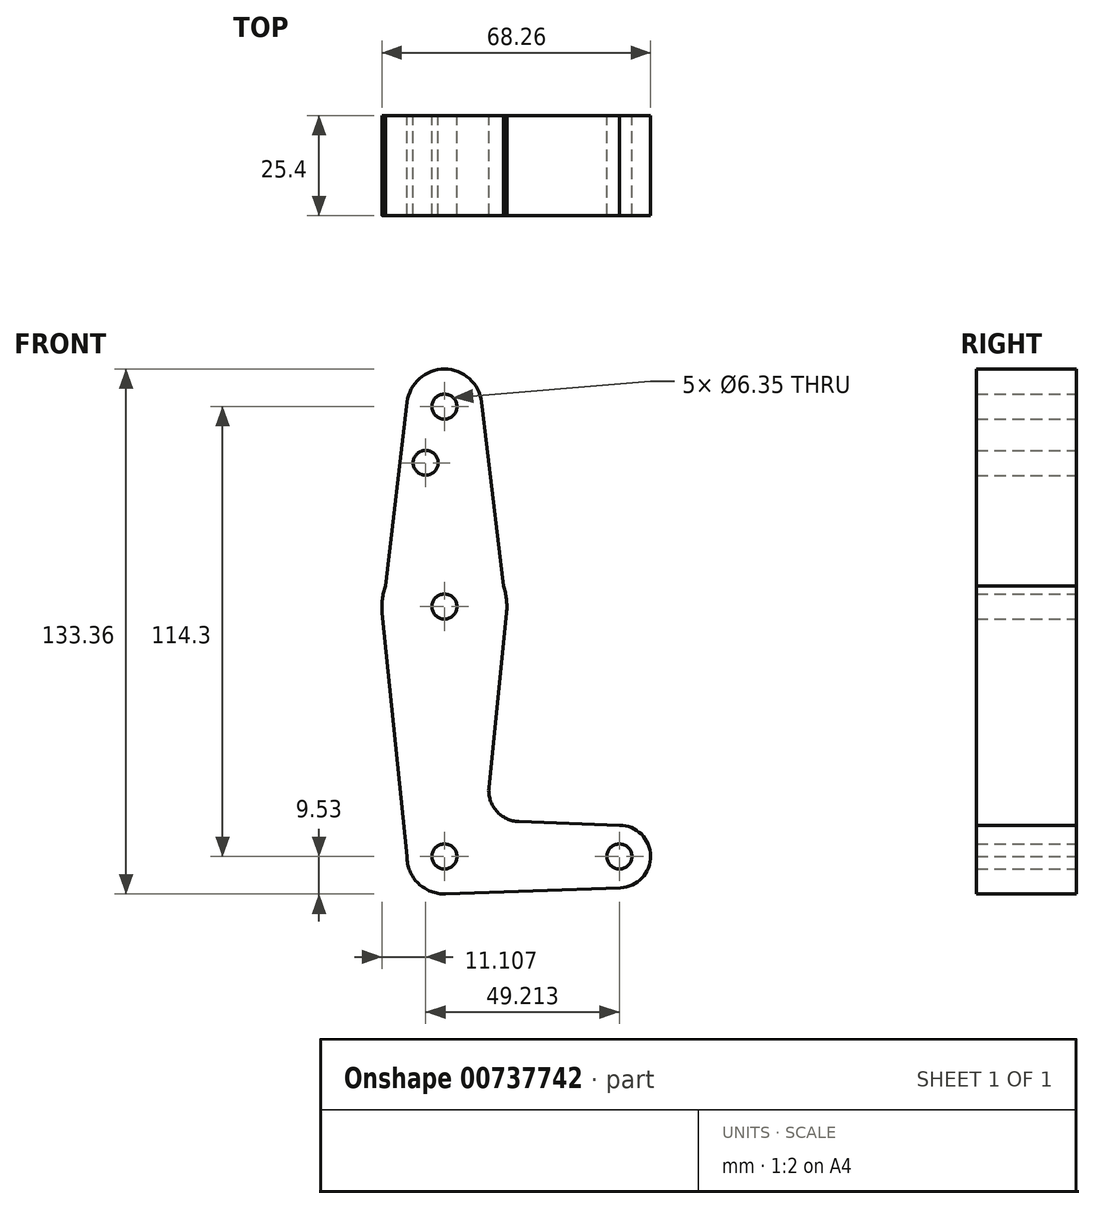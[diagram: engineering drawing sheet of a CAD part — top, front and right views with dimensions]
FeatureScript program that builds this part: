
annotation { "Feature Type Name" : "Feature", "Feature Type Description" : "" }
export const myFeature = defineFeature(function(context is Context, id is Id, definition is map)
    precondition{}
    {
        {
            var Q0;
            Q0=qCreatedBy(makeId("Front.planeOp"),FACE);
            var sketch = newSketch(context, id + "F0", { "sketchPlane" : qUnion([Q0])});
            skLineSegment(sketch, "E0", {"start": v(0, 0) * mm, "end": v(44.45, 0) * mm, "construction": true});
            skCircle(sketch, "E1", {"center": v(44.45, 0) * mm, "radius": 7.94 * mm});
            skPoint(sketch, "E2.orphan", {"position": v(0, 57.15) * mm});
            skPoint(sketch, "E3.center.orphan", {"position": v(0, 114.3) * mm});
            skLineSegment(sketch, "E4", {"start": v(0, 114.3) * mm, "end": v(0, 0) * mm, "construction": true});
            skCircle(sketch, "E5", {"center": v(0, 0) * mm, "radius": 9.53 * mm});
            skCircle(sketch, "E6", {"center": v(0, 114.3) * mm, "radius": 9.53 * mm});
            skPoint(sketch, "E7.orphan", {"position": v(0, -6.35) * mm});
            skCircle(sketch, "E8", {"center": v(0, 63.5) * mm, "radius": 15.88 * mm});
            skLineSegment(sketch, "E9", {"start": v(44.45, 7.94) * mm, "end": v(18.93, 8.85) * mm});
            skLineSegment(sketch, "E10", {"start": v(44.73, -7.93) * mm, "end": v(0, -9.53) * mm});
            skLineSegment(sketch, "E11", {"start": v(11.3, 17.6) * mm, "end": v(15.8, 61.9) * mm});
            skLineSegment(sketch, "E12", {"start": v(-9.52, 0) * mm, "end": v(-15.8, 61.9) * mm});
            skLineSegment(sketch, "E13", {"start": v(-15.8, 61.9) * mm, "end": v(-9.46, 115.42) * mm});
            skLineSegment(sketch, "E14", {"start": v(9.46, 115.42) * mm, "end": v(15.8, 61.9) * mm});
            skCircle(sketch, "E15", {"center": v(0, 114.3) * mm, "radius": 3.18 * mm});
            skCircle(sketch, "E16", {"center": v(-4.76, 100.03) * mm, "radius": 3.18 * mm});
            skCircle(sketch, "E17", {"center": v(0, 63.5) * mm, "radius": 3.18 * mm});
            skCircle(sketch, "E18", {"center": v(0, 0) * mm, "radius": 3.18 * mm});
            skCircle(sketch, "E19", {"center": v(44.45, 0) * mm, "radius": 3.18 * mm});
            skArc(sketch, "E20.filletArc", {"start": v(11.3, 17.6) * mm, "mid": v(13.22, 11.57) * mm, "end": v(18.93, 8.85) * mm});
            skSolve(sketch);
        }
        {
            var Q0;
            Q0 = qSketchRegion(id + "F0", true);
            extrude(context, id + "F1", {"entities" : qUnion([Q0]), "depth" : 25.4 * mm, "offsetDistance" : 25.4 * mm});
        }
    });
